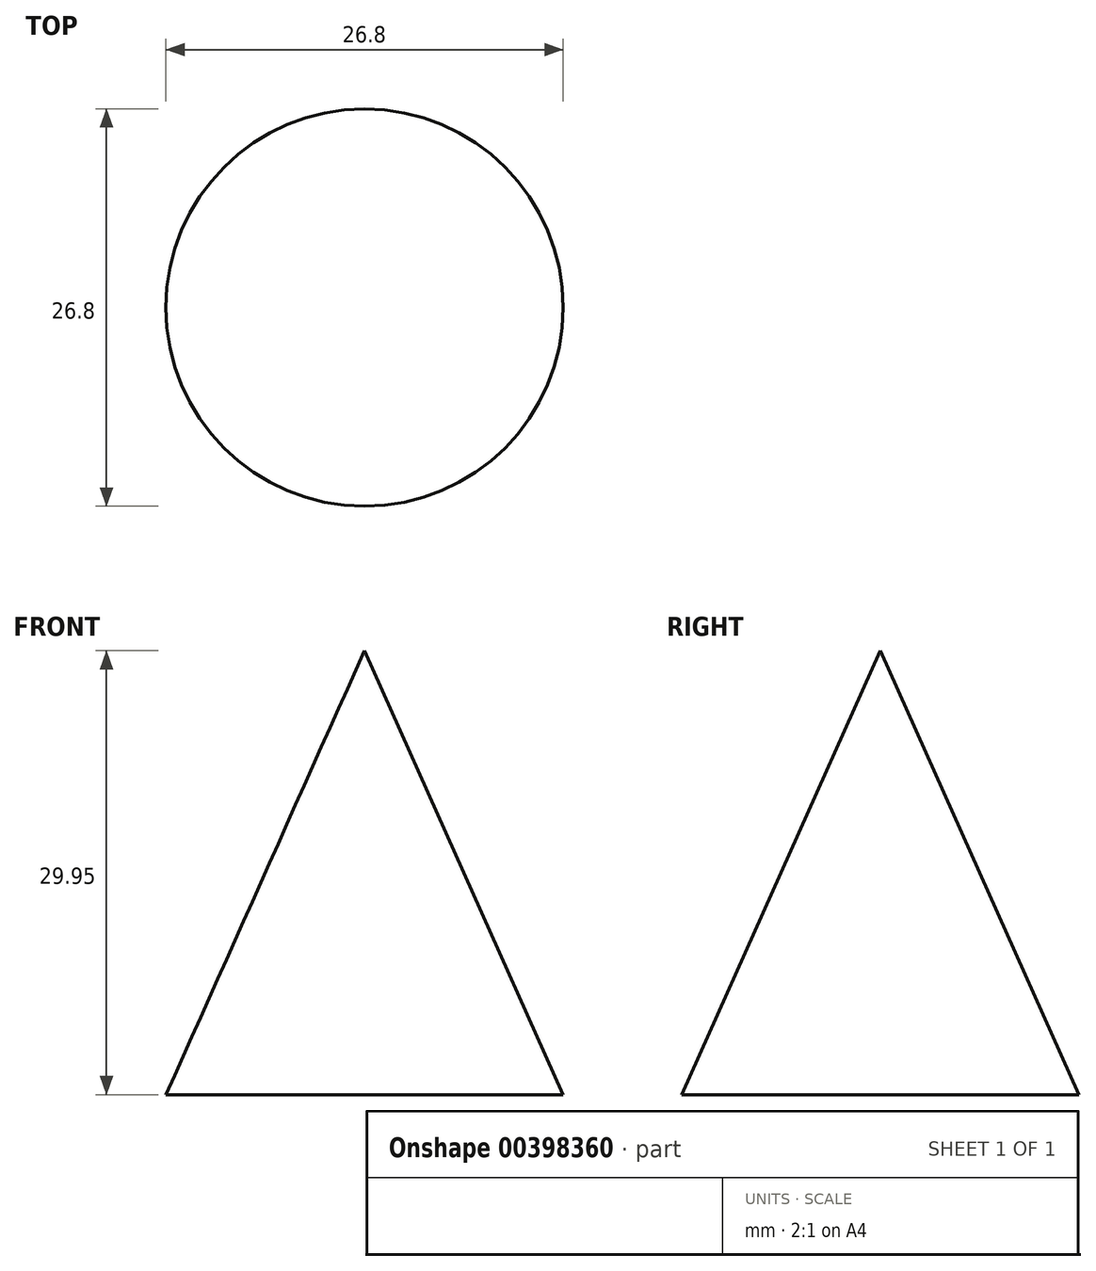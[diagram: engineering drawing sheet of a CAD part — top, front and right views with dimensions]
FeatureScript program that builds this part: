
annotation { "Feature Type Name" : "Feature", "Feature Type Description" : "" }
export const myFeature = defineFeature(function(context is Context, id is Id, definition is map)
    precondition{}
    {
        {
            var Q0;
            Q0=qCreatedBy(makeId("Front.planeOp"),FACE);
            var sketch = newSketch(context, id + "F0", { "sketchPlane" : qUnion([Q0])});
            skLineSegment(sketch, "E0", {"start": v(0, 0) * mm, "end": v(-13.4, -29.95) * mm});
            skLineSegment(sketch, "E1", {"start": v(-13.4, -29.95) * mm, "end": v(0, -29.95) * mm});
            skLineSegment(sketch, "E2", {"start": v(0, -29.95) * mm, "end": v(0, 0) * mm});
            skSolve(sketch);
        }
        {
            var Q0;
            Q0=makeQuery(id+"F0.imprint","IMPRINT",FACE,{"disambiguationData":[TD([[makeQuery(id+"F0.imprint","IMPRINT",EDGE,{"derivedFrom":sQuery(id+"F0.wireOp",EDGE,"E0")}),1.0]])]});
            var Q1;
            Q1=sQuery(id+"F0.wireOp",EDGE,"E2");
            revolve(context, id + "F1", {"entities" : qUnion([Q0]), "axis" : qUnion([Q1]), "revolveType" : RevolveType.FULL});
        }
    });
